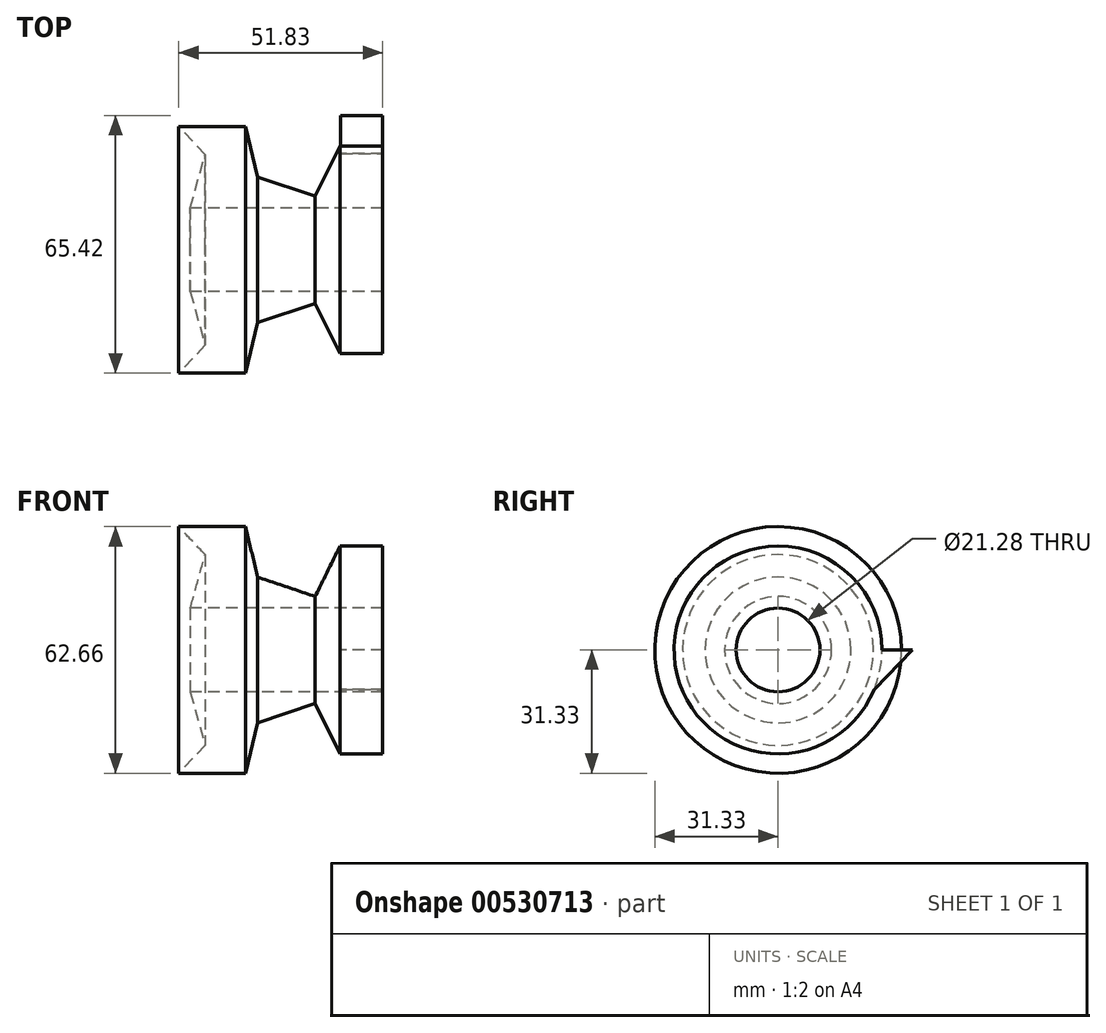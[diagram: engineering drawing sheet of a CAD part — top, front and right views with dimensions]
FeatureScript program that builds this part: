
annotation { "Feature Type Name" : "Feature", "Feature Type Description" : "" }
export const myFeature = defineFeature(function(context is Context, id is Id, definition is map)
    precondition{}
    {
        {
            var Q0;
            Q0=qCreatedBy(makeId("Front.planeOp"),FACE);
            var sketch = newSketch(context, id + "F0", { "sketchPlane" : qUnion([Q0])});
            skLineSegment(sketch, "E0", {"start": v(-48.87, 10.64) * mm, "end": v(-45.13, 24.24) * mm});
            skLineSegment(sketch, "E1", {"start": v(-45.13, 24.24) * mm, "end": v(-51.83, 31.33) * mm});
            skLineSegment(sketch, "E2", {"start": v(-51.83, 31.33) * mm, "end": v(-34.88, 31.33) * mm});
            skLineSegment(sketch, "E3", {"start": v(-34.88, 31.33) * mm, "end": v(-31.73, 18.52) * mm});
            skLineSegment(sketch, "E4", {"start": v(-31.73, 18.52) * mm, "end": v(-17.15, 13.6) * mm});
            skLineSegment(sketch, "E5", {"start": v(-17.15, 13.6) * mm, "end": v(-10.84, 26.4) * mm});
            skLineSegment(sketch, "E6", {"start": v(-10.84, 26.4) * mm, "end": v(0, 26.4) * mm});
            skLineSegment(sketch, "E7", {"start": v(0, 26.4) * mm, "end": v(0, 10.64) * mm});
            skLineSegment(sketch, "E8", {"start": v(0, 10.64) * mm, "end": v(-48.87, 10.64) * mm});
            skSolve(sketch);
        }
        {
            var Q0;
            Q0=qCreatedBy(makeId("Front.planeOp"),FACE);
            var sketch = newSketch(context, id + "F1", { "sketchPlane" : qUnion([Q0])});
            skLineSegment(sketch, "E9", {"start": v(-53.2, 0) * mm, "end": v(0, 0) * mm});
            skSolve(sketch);
        }
        {
            var Q0;
            Q0=makeQuery(id+"F0.imprint","IMPRINT",FACE,{"disambiguationData":[TD([[makeQuery(id+"F0.imprint","IMPRINT",EDGE,{"derivedFrom":sQuery(id+"F0.wireOp",EDGE,"E0")}),-1.0]])]});
            var Q1;
            Q1=sQuery(id+"F1.wireOp",EDGE,"E9");
            revolve(context, id + "F2", {"entities" : qUnion([Q0]), "axis" : qUnion([Q1]), "revolveType" : RevolveType.FULL});
        }
        {
            var Q0;
            Q0=qCreatedBy(makeId("Right.planeOp"),FACE);
            var sketch = newSketch(context, id + "F3", { "sketchPlane" : qUnion([Q0])});
            skLineSegment(sketch, "E10", {"start": v(25.82, 0) * mm, "end": v(34.1, 0) * mm});
            skLineSegment(sketch, "E11", {"start": v(34.1, 0) * mm, "end": v(24.44, -10.05) * mm});
            skLineSegment(sketch, "E12", {"start": v(25.82, 0) * mm, "end": v(24.44, -10.05) * mm});
            skSolve(sketch);
        }
        {
            var Q0;
            Q0=makeQuery(id+"F3.imprint","IMPRINT",FACE,{"disambiguationData":[TD([[makeQuery(id+"F3.imprint","IMPRINT",EDGE,{"derivedFrom":sQuery(id+"F3.wireOp",EDGE,"E10")}),-1.0]])]});
            extrude(context, id + "F4", {"entities" : qUnion([Q0]), "operationType" : NewBodyOperationType.ADD, "oppositeDirection" : true, "depth" : 10.67 * mm, "offsetDistance" : 25.4 * mm});
        }
    });
